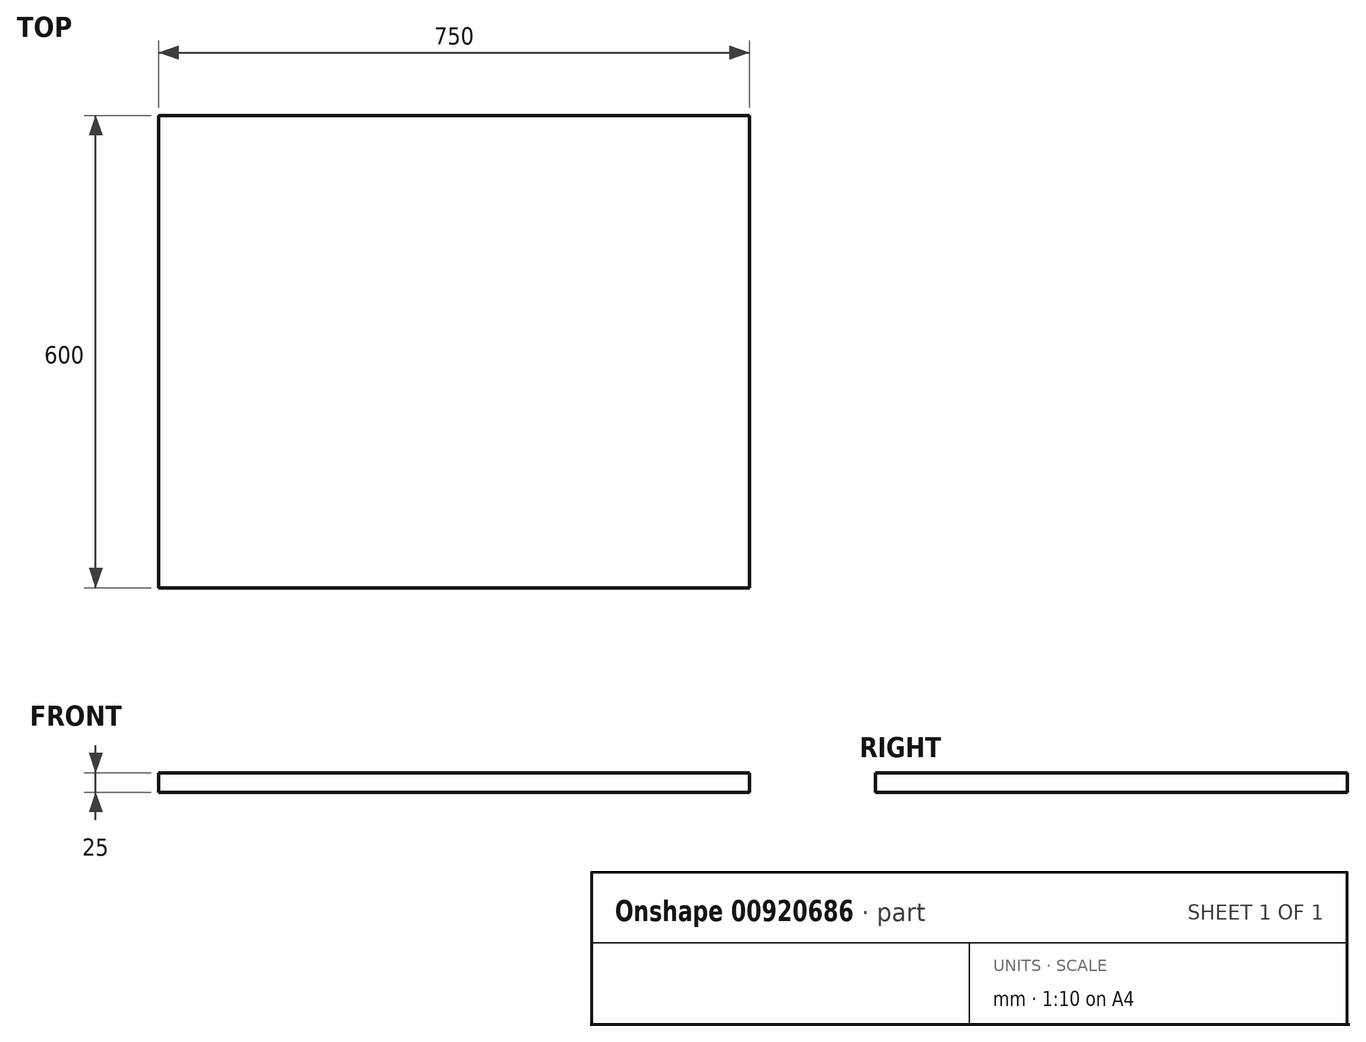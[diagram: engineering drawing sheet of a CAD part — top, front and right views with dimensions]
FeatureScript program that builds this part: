
annotation { "Feature Type Name" : "Feature", "Feature Type Description" : "" }
export const myFeature = defineFeature(function(context is Context, id is Id, definition is map)
    precondition{}
    {
        {
            var Q0;
            Q0=qCreatedBy(makeId("Top.planeOp"),FACE);
            var sketch = newSketch(context, id + "F0", { "sketchPlane" : qUnion([Q0])});
            skLineSegment(sketch, "E0.bottom", {"start": v(0, 0) * mm, "end": v(750, 0) * mm});
            skLineSegment(sketch, "E0.top", {"start": v(0, 600) * mm, "end": v(750, 600) * mm});
            skLineSegment(sketch, "E0.left", {"start": v(0, 0) * mm, "end": v(0, 600) * mm});
            skLineSegment(sketch, "E0.right", {"start": v(750, 0) * mm, "end": v(750, 600) * mm});
            skSolve(sketch);
        }
        {
            var Q0;
            Q0=makeQuery(id+"F0.imprint","IMPRINT",FACE,{"disambiguationData":[TD([[makeQuery(id+"F0.imprint","IMPRINT",EDGE,{"derivedFrom":sQuery(id+"F0.wireOp",EDGE,"E0.bottom")}),1.0]])]});
            extrude(context, id + "F1", {"entities" : qUnion([Q0]), "depth" : 25 * mm, "offsetDistance" : 25 * mm});
        }
    });
